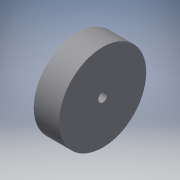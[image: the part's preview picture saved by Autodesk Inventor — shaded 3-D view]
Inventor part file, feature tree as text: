
AUTODESK INVENTOR PART (.ipt)
format: ipt  version: 2017 SP1 (Build 210196100, 196)  size: 96,256 bytes
history: native  units: in
note: dims shown in document units (in); Inventor stores cm internally (conversion verified against a paired STEP export)
features: extrude x1, sketch x1
ambient origin geometry x8: Origin, YZ Plane, XZ Plane, XY Plane, X Axis, Y Axis, Z Axis, Center Point
bodies: Solid1 (feature_tree)
feature tree (2):
  extrude  "Extrusion1"  Depth=1.75in
  sketch  "Sketch1"  dims[d0=6.0in d1=0.625in d2=1.75in d3=0.0in]
